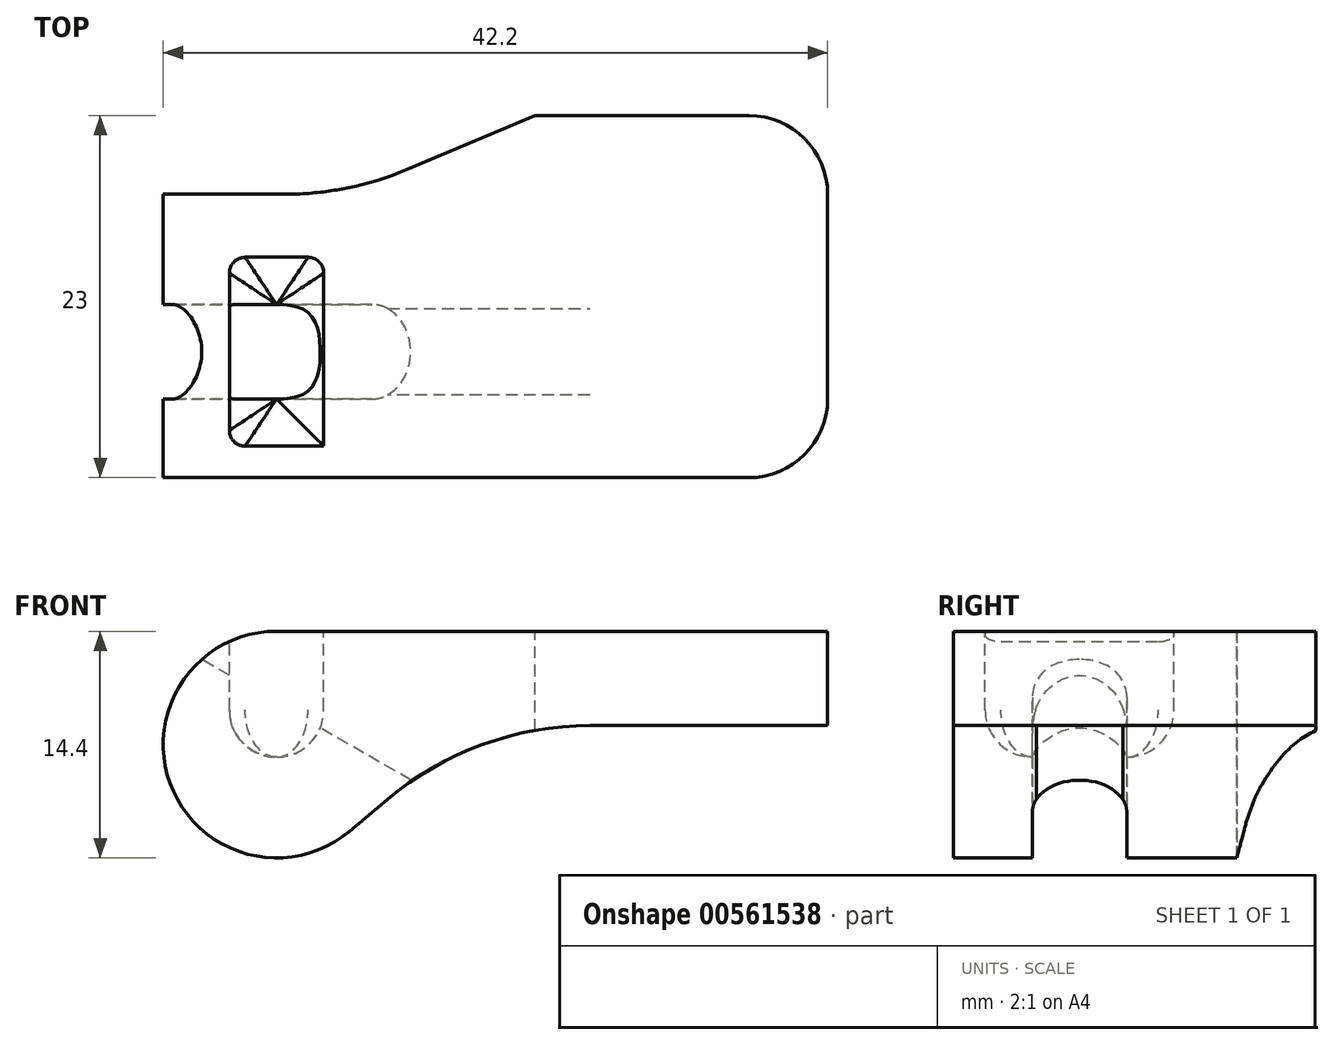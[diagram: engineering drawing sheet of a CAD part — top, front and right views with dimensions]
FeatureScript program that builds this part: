
annotation { "Feature Type Name" : "Feature", "Feature Type Description" : "" }
export const myFeature = defineFeature(function(context is Context, id is Id, definition is map)
    precondition{}
    {
        {
            var Q0;
            Q0=qCreatedBy(makeId("Front.planeOp"),FACE);
            var sketch = newSketch(context, id + "F0", { "sketchPlane" : qUnion([Q0])});
            skCircle(sketch, "E0", {"center": v(0, 0) * mm, "radius": 7.2 * mm});
            skLineSegment(sketch, "E1.bottom", {"start": v(0, 7.2) * mm, "end": v(35, 7.2) * mm});
            skLineSegment(sketch, "E1.left", {"start": v(0, 7.2) * mm, "end": v(0, -7.2) * mm});
            skLineSegment(sketch, "E1.right", {"start": v(35, 7.2) * mm, "end": v(35, 1.2) * mm});
            skLineSegment(sketch, "E2", {"start": v(4.63, -5.52) * mm, "end": v(12.63, 1.2) * mm});
            skLineSegment(sketch, "E3", {"start": v(12.63, 1.2) * mm, "end": v(35, 1.2) * mm});
            skSolve(sketch);
        }
        {
            var Q0;
            Q0 = qSketchRegion(id + "F0", true);
            extrude(context, id + "F1", {"entities" : qUnion([Q0]), "depth" : 23 * mm, "offsetDistance" : 25 * mm});
        }
        {
            var Q0;
            Q0=makeQuery(id+"F1.opExtrude","SWEPT_FACE",FACE,{"disambiguationData":[OSD([sQuery(id+"F0.wireOp",EDGE,"E1.bottom")])]});
            var sketch = newSketch(context, id + "F2", { "sketchPlane" : qUnion([Q0])});
            skLineSegment(sketch, "E4.bottom", {"start": v(-3, -9) * mm, "end": v(3, -9) * mm});
            skLineSegment(sketch, "E4.top", {"start": v(-3, -21) * mm, "end": v(3, -21) * mm});
            skLineSegment(sketch, "E4.left", {"start": v(-3, -9) * mm, "end": v(-3, -21) * mm});
            skLineSegment(sketch, "E4.right", {"start": v(3, -9) * mm, "end": v(3, -21) * mm});
            skSolve(sketch);
        }
        {
            var Q0;
            Q0 = qSketchRegion(id + "F2", true);
            extrude(context, id + "F3", {"entities" : qUnion([Q0]), "operationType" : NewBodyOperationType.REMOVE, "oppositeDirection" : true, "depth" : 8 * mm, "offsetDistance" : 25 * mm});
        }
        {
            var Q0;
            Q0=makeQuery(id+"F1.opExtrude","SWEPT_FACE",FACE,{"disambiguationData":[OSD([sQuery(id+"F0.wireOp",EDGE,"E0")])]});
            cPlane(context, id + "F4", {"entities" : qUnion([Q0]), "cplaneType" : CPlaneType.LINE_ANGLE, "offset" : 25 * mm, "angle" : 120 * degree, "width" : 150 * mm, "height" : 150 * mm});
        }
        {
            var Q0;
            Q0=qCreatedBy(id+"F4.planeOp",FACE);
            var sketch = newSketch(context, id + "F5", { "sketchPlane" : qUnion([Q0])});
            skLineSegment(sketch, "E5", {"start": v(0, 0) * mm, "end": v(-30.85, 0) * mm, "construction": true});
            skLineSegment(sketch, "E6.bottom", {"start": v(-12, -12.23) * mm, "end": v(-18, -12.23) * mm});
            skLineSegment(sketch, "E6.top", {"start": v(-12, 2.3) * mm, "end": v(-18, 2.3) * mm});
            skLineSegment(sketch, "E6.left", {"start": v(-12, -12.23) * mm, "end": v(-12, 2.3) * mm});
            skLineSegment(sketch, "E6.right", {"start": v(-18, -12.23) * mm, "end": v(-18, 2.3) * mm});
            skLineSegment(sketch, "E7", {"start": v(-15, 10.85) * mm, "end": v(-15, -10.3) * mm, "construction": true});
            skSolve(sketch);
        }
        {
            var Q0;
            Q0=makeQuery(id+"F5.imprint","IMPRINT",FACE,{"disambiguationData":[TD([[makeQuery(id+"F5.imprint","IMPRINT",EDGE,{"derivedFrom":sQuery(id+"F5.wireOp",EDGE,"E6.bottom")}),-1.0]])]});
            extrude(context, id + "F6", {"entities" : qUnion([Q0]), "operationType" : NewBodyOperationType.REMOVE, "oppositeDirection" : true, "depth" : 25 * mm, "offsetDistance" : 25 * mm, "hasSecondDirection" : true, "secondDirectionOppositeDirection" : false, "secondDirectionDepth" : 25 * mm});
        }
        {
            var Q0;
            {var subQ0=sQuery(id+"F5.wireOp",EDGE,"E6.top");var subQ1=sQuery(id+"F5.wireOp",EDGE,"E6.left");Q0=makeQuery(id+"F6.boolean.opBoolean","COPY",EDGE,{"disambiguationData":[TD([makeQuery(id+"F1.opExtrude","SWEPT_FACE",FACE,{"disambiguationData":[OSD([sQuery(id+"F0.wireOp",EDGE,"E0")])]})])],"derivedFrom":makeQuery(id+"F6.opExtrude","SWEPT_EDGE",EDGE,{"disambiguationData":[OSD([subQ0,subQ1])]})});}
            var Q1;
            {var subQ0=sQuery(id+"F5.wireOp",EDGE,"E6.top");var subQ1=sQuery(id+"F5.wireOp",EDGE,"E6.right");Q1=makeQuery(id+"F6.boolean.opBoolean","COPY",EDGE,{"disambiguationData":[TD([makeQuery(id+"F1.opExtrude","SWEPT_FACE",FACE,{"disambiguationData":[OSD([sQuery(id+"F0.wireOp",EDGE,"E0")])]})])],"derivedFrom":makeQuery(id+"F6.opExtrude","SWEPT_EDGE",EDGE,{"disambiguationData":[OSD([subQ0,subQ1])]})});}
            fillet(context, id + "F7", {"entities" : qUnion([Q0, Q1]), "radius" : 3 * mm, "tangentPropagation" : true, "allowEdgeOverflow" : false});
        }
        {
            var Q0;
            {var subQ0=sQuery(id+"F5.wireOp",EDGE,"E6.top");var subQ1=sQuery(id+"F5.wireOp",EDGE,"E6.left");Q0=makeQuery(id+"F6.boolean.opBoolean","COPY",EDGE,{"disambiguationData":[TD([makeQuery(id+"F1.opExtrude","SWEPT_FACE",FACE,{"disambiguationData":[OSD([sQuery(id+"F0.wireOp",EDGE,"E2")])]})])],"derivedFrom":makeQuery(id+"F6.opExtrude","SWEPT_EDGE",EDGE,{"disambiguationData":[OSD([subQ0,subQ1])]})});}
            var Q1;
            {var subQ0=sQuery(id+"F5.wireOp",EDGE,"E6.top");var subQ1=sQuery(id+"F5.wireOp",EDGE,"E6.right");Q1=makeQuery(id+"F6.boolean.opBoolean","COPY",EDGE,{"disambiguationData":[TD([makeQuery(id+"F1.opExtrude","SWEPT_FACE",FACE,{"disambiguationData":[OSD([sQuery(id+"F0.wireOp",EDGE,"E2")])]})])],"derivedFrom":makeQuery(id+"F6.opExtrude","SWEPT_EDGE",EDGE,{"disambiguationData":[OSD([subQ0,subQ1])]})});}
            fillet(context, id + "F8", {"entities" : qUnion([Q0, Q1]), "radius" : 3 * mm, "tangentPropagation" : true, "allowEdgeOverflow" : false});
        }
        {
            var Q0;
            Q0=makeQuery(id+"F1.opExtrude","CAP_EDGE",EDGE,{"disambiguationData":[OSD([sQuery(id+"F0.wireOp",EDGE,"E1.right")])],"isStart":false});
            var Q1;
            Q1=makeQuery(id+"F1.opExtrude","CAP_EDGE",EDGE,{"disambiguationData":[OSD([sQuery(id+"F0.wireOp",EDGE,"E1.right")])],"isStart":true});
            fillet(context, id + "F9", {"entities" : qUnion([Q0, Q1]), "radius" : 5 * mm, "tangentPropagation" : true, "allowEdgeOverflow" : false});
        }
        {
            var Q0;
            Q0=makeQuery(id+"F1.opExtrude","SWEPT_EDGE",EDGE,{"disambiguationData":[OSD([sQuery(id+"F0.wireOp",EDGE,"E2"),sQuery(id+"F0.wireOp",EDGE,"E3")])]});
            fillet(context, id + "F10", {"entities" : qUnion([Q0]), "radius" : 20 * mm, "tangentPropagation" : true, "allowEdgeOverflow" : false});
        }
        {
            var Q0;
            Q0=makeQuery(id+"F3.boolean.opBoolean","COPY",EDGE,{"derivedFrom":makeQuery(id+"F3.opExtrude","SWEPT_EDGE",EDGE,{"disambiguationData":[OSD([sQuery(id+"F2.wireOp",EDGE,"E4.bottom"),sQuery(id+"F2.wireOp",EDGE,"E4.left")])]})});
            var Q1;
            Q1=makeQuery(id+"F3.boolean.opBoolean","COPY",EDGE,{"derivedFrom":makeQuery(id+"F3.opExtrude","SWEPT_EDGE",EDGE,{"disambiguationData":[OSD([sQuery(id+"F2.wireOp",EDGE,"E4.bottom"),sQuery(id+"F2.wireOp",EDGE,"E4.right")])]})});
            var Q2;
            Q2=makeQuery(id+"F3.boolean.opBoolean","COPY",EDGE,{"derivedFrom":makeQuery(id+"F3.opExtrude","SWEPT_EDGE",EDGE,{"disambiguationData":[OSD([sQuery(id+"F2.wireOp",EDGE,"E4.top"),sQuery(id+"F2.wireOp",EDGE,"E4.left")])]})});
            fillet(context, id + "F11", {"entities" : qUnion([Q0, Q1, Q2]), "radius" : 1 * mm, "tangentPropagation" : true, "allowEdgeOverflow" : false});
        }
        {
            var Q0;
            Q0=qCreatedBy(makeId("Top.planeOp"),FACE);
            var sketch = newSketch(context, id + "F12", { "sketchPlane" : qUnion([Q0])});
            skLineSegment(sketch, "E8", {"start": v(-7.47, -5) * mm, "end": v(4.53, -5) * mm});
            skLineSegment(sketch, "E9", {"start": v(4.53, -5) * mm, "end": v(16.4, 0) * mm});
            skLineSegment(sketch, "E10", {"start": v(16.4, 0) * mm, "end": v(-7.45, 0) * mm});
            skLineSegment(sketch, "E11", {"start": v(-7.45, 0) * mm, "end": v(-7.47, -5) * mm});
            skSolve(sketch);
        }
        {
            var Q0;
            Q0=makeQuery(id+"F3.boolean.opBoolean","COPY",EDGE,{"derivedFrom":makeQuery(id+"F3.opExtrude","CAP_EDGE",EDGE,{"disambiguationData":[OSD([sQuery(id+"F2.wireOp",EDGE,"E4.right")])],"isStart":false})});
            var Q1;
            Q1=makeQuery(id+"F3.boolean.opBoolean","COPY",EDGE,{"derivedFrom":makeQuery(id+"F3.opExtrude","CAP_EDGE",EDGE,{"disambiguationData":[OSD([sQuery(id+"F2.wireOp",EDGE,"E4.left")])],"isStart":false})});
            fillet(context, id + "F13", {"entities" : qUnion([Q0, Q1]), "radius" : 3 * mm, "tangentPropagation" : true, "allowEdgeOverflow" : false});
        }
        {
            var Q0;
            Q0 = qSketchRegion(id + "F12", true);
            extrude(context, id + "F14", {"entities" : qUnion([Q0]), "operationType" : NewBodyOperationType.REMOVE, "oppositeDirection" : true, "depth" : 25 * mm, "offsetDistance" : 25 * mm, "hasSecondDirection" : true, "secondDirectionOppositeDirection" : false, "secondDirectionDepth" : 25 * mm});
        }
        {
            var Q0;
            Q0=makeQuery(id+"F14.boolean.opBoolean","COPY",EDGE,{"derivedFrom":makeQuery(id+"F14.opExtrude","SWEPT_EDGE",EDGE,{"disambiguationData":[OSD([sQuery(id+"F12.wireOp",EDGE,"E8"),sQuery(id+"F12.wireOp",EDGE,"E9")])]})});
            var Q1;
            Q1=makeQuery(id+"F14.boolean.opBoolean","COPY",EDGE,{"derivedFrom":makeQuery(id+"F14.opExtrude","SWEPT_EDGE",EDGE,{"disambiguationData":[OSD([sQuery(id+"F12.wireOp",EDGE,"E9"),sQuery(id+"F12.wireOp",EDGE,"E10")])]})});
            fillet(context, id + "F15", {"entities" : qUnion([Q0, Q1]), "radius" : 20 * mm, "tangentPropagation" : true, "allowEdgeOverflow" : false});
        }
    });
